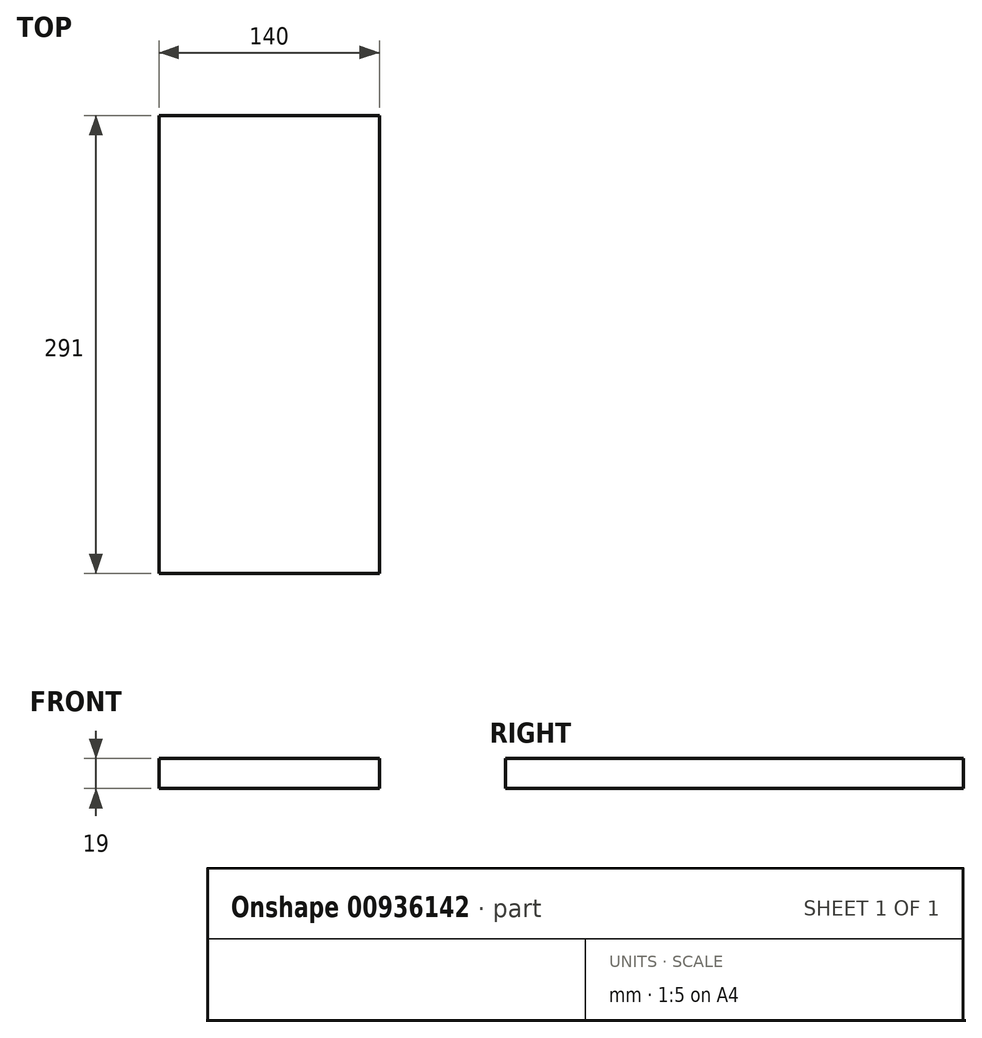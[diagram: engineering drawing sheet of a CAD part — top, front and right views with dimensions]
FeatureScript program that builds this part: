
annotation { "Feature Type Name" : "Feature", "Feature Type Description" : "" }
export const myFeature = defineFeature(function(context is Context, id is Id, definition is map)
    precondition{}
    {
        {
            var Q0;
            Q0=qCreatedBy(makeId("Front.planeOp"),FACE);
            var sketch = newSketch(context, id + "F0", { "sketchPlane" : qUnion([Q0])});
            skLineSegment(sketch, "E0.bottom", {"start": v(0, 0) * mm, "end": v(140, 0) * mm});
            skLineSegment(sketch, "E0.top", {"start": v(0, 19) * mm, "end": v(140, 19) * mm});
            skLineSegment(sketch, "E0.left", {"start": v(0, 0) * mm, "end": v(0, 19) * mm});
            skLineSegment(sketch, "E0.right", {"start": v(140, 0) * mm, "end": v(140, 19) * mm});
            skSolve(sketch);
        }
        {
            var Q0;
            Q0=makeQuery(id+"F0.imprint","IMPRINT",FACE,{"disambiguationData":[TD([[makeQuery(id+"F0.imprint","IMPRINT",EDGE,{"derivedFrom":sQuery(id+"F0.wireOp",EDGE,"E0.bottom")}),1.0]])]});
            extrude(context, id + "F1", {"entities" : qUnion([Q0]), "depth" : 291 * mm, "offsetDistance" : 25 * mm});
        }
    });
